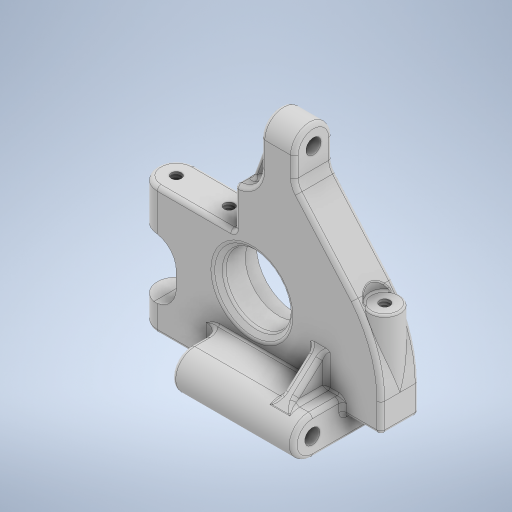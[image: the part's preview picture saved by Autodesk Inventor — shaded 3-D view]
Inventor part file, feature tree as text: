
AUTODESK INVENTOR PART (.ipt)
format: ipt  version: 2024 (Build 280153000, 153)  size: 982,016 bytes
history: native  units: in
note: dims shown in document units (in); Inventor stores cm internally (conversion verified against a paired STEP export)
features: fillet x19, sketch x19, extrude x13, plane x8, projected_geometry x6, hole x4, other x2, rib x2, chamfer x1
ambient origin geometry x8: Origin, YZ Plane, XZ Plane, XY Plane, X Axis, Y Axis, Z Axis, Center Point
bodies: Solid1 (feature_tree)
feature tree (74):
  extrude  "Extrusion1"  Depth=0.215in
  extrude  "Extrusion2"  Depth=0.5in
  fillet  "Fillet1"  Radius=0.315in
  extrude  "Extrusion3"  Depth=0.425in
  extrude  "Extrusion4"  Depth=1.825in
  extrude  "Extrusion5"  TaperAngle=120.0deg  [1 undecoded]
  extrude  "Extrusion6"  Depth=1.0in
  extrude  "Extrusion7"  Depth=0.315in TaperAngle=0.0deg
  fillet  "Fillet2"  Radius=0.315in
  extrude  "Extrusion8"  TaperAngle=0.0deg  [1 undecoded]
  chamfer  "Chamfer1"  Distance=0.315in
  fillet  "Fillet3"  Radius=0.276in
  fillet  "Fillet4"  Radius=0.315in
  fillet  "Fillet5"  Radius=0.75in
  fillet  "Fillet6"  Radius=0.6825in
  fillet  "Fillet7"  Radius=1.0625in
  fillet  "Fillet8"  Radius=0.035in
  fillet  "Fillet9"  Radius=0.625in
  other  "Work Point1"
  plane  "Work Plane1"
  other  "Work Axis1"
  plane  "Work Plane5"
  extrude  "Extrusion9"  Depth=0.032in
  fillet  "Fillet10"  Radius=0.55in
  fillet  "Fillet11"  [1 undecoded]
  fillet  "Fillet12"  Radius=0.1875in
  fillet  "Fillet13"  Radius=0.032in
  hole  "Hole1"  [1 undecoded]
  plane  "Work Plane6"
  rib  "Rib1"
  fillet  "Fillet14"  Radius=0.032in
  plane  "Work Plane7"
  extrude  "Extrusion10"  Depth=0.032in
  extrude  "Extrusion11"  [1 undecoded]
  fillet  "Fillet15"  [1 undecoded]
  hole  "Hole2"  [1 undecoded]
  plane  "Work Plane8"
  rib  "Rib2"
  fillet  "Fillet16"  Radius=1.0in
  fillet  "Fillet17"  Radius=0.032in
  fillet  "Fillet18"  Radius=0.125in
  extrude  "Extrusion12"  Depth=0.015in
  extrude  "Extrusion13"  [1 undecoded]
  fillet  "Fillet19"  Radius=0.1in
  hole  "Hole3"  [1 undecoded]
  hole  "Hole4"  [1 undecoded]
  sketch  "Sketch1"  dims[d0=2.0in d1=0.215in]
  sketch  "Sketch2"  dims[d2=0.315in d3=0.5in d4=0.315in]
  sketch  "Sketch3"  dims[d5=1.05in d6=0.425in]
  sketch  "Sketch4"  dims[d7=0.2762in d8=1.825in]
  sketch  "Sketch5"  dims[d9=0.361in d10=120.0deg]
  sketch  "Sketch6"  dims[d11=0.3356in d12=1.0in]
  sketch  "Sketch7"  dims[d13=0.989in d14=0.315in d15=0.0in d16=0.315in]
  sketch  "Sketch8"  dims[d17=0.1875in d18=0.0in d19=0.0in]
  plane  "Work Plane2"
  plane  "Work Plane3"
  plane  "Work Plane4"
  sketch  "Sketch10"  dims[d20=0.1575in]
  sketch  "Sketch11"  dims[d21=0.795in]
  sketch  "Sketch12"  dims[d22=0.3438in d23=0.315in d24=0.0in d25=0.276in d26=0.0in d27=0.315in d28=0.0in d29=0.75in d30=0.6825in d31=1.0625in d32=0.035in d33=0.0in d34=0.625in]
  sketch  "Sketch13"  dims[d35=0.1288in d36=0.0in d37=0.032in d38=0.55in d39=0.0in d40=0.0in]
  sketch  "Sketch14"  dims[d41=0.05in d42=0.125in d43=45.0deg d44=0.1875in d45=0.032in]
  sketch  "Sketch16"  dims[d46=0.032in d47=0.125in d48=0.032in]
  sketch  "Sketch17"  dims[d49=0.015in d50=0.032in]
  sketch  "Sketch18"  dims[d51=0.25in d52=-0.1575in d53=-1.0in]
  sketch  "Sketch19"  dims[d54=0.315in d55=0.25in d56=1.0in d57=0.0in d58=0.032in d59=0.125in]
  sketch  "Sketch20"  dims[d60=0.032in d61=0.015in]
  sketch  "Sketch21"  dims[d62=0.125in d63=0.75in d64=0.375in d65=0.25in d66=0.5635in d67=0.7874in d68=0.8108in d69=-0.5in d70=0.1in d71=0.1in d72=0.0in d73=0.0in d74=0.1in d75=0.1in d76=0.032in d77=-1.0in d78=0.25in d79=1.0in d80=0.0in d81=0.25in d82=0.0in d83=0.0in d84=0.015in d85=0.0849in d86=0.224in d87=0.375in d88=0.25in d89=0.5635in d90=0.315in d91=0.8108in d92=0.1in d93=0.1in d94=0.0in d95=0.0in d96=0.1in d97=0.1in d98=0.032in d99=0.032in d100=0.032in d101=0.22in d102=1.0in d103=0.0in d104=0.15in d105=0.0in d106=0.015in d107=0.125in d108=0.224in d109=0.375in d110=0.25in d111=0.5635in d112=0.349in d113=0.8108in d114=0.435in d115=0.0849in d116=0.224in d117=0.375in d118=0.25in d119=0.5635in d120=0.315in d121=0.8108in]
  projected_geometry  "Project Cut Edges1"
  projected_geometry  "Project Cut Edges2"
  projected_geometry  "Project Cut Edges3"
  projected_geometry  "Project Cut Edges4"
  projected_geometry  "Project Cut Edges5"
  projected_geometry  "Project Cut Edges6"
note: 10 required parameter values undecoded (feature->parameter linkage not recoverable at this tier; creation-order binding heuristic only, values carry confidence <= 0.55)
